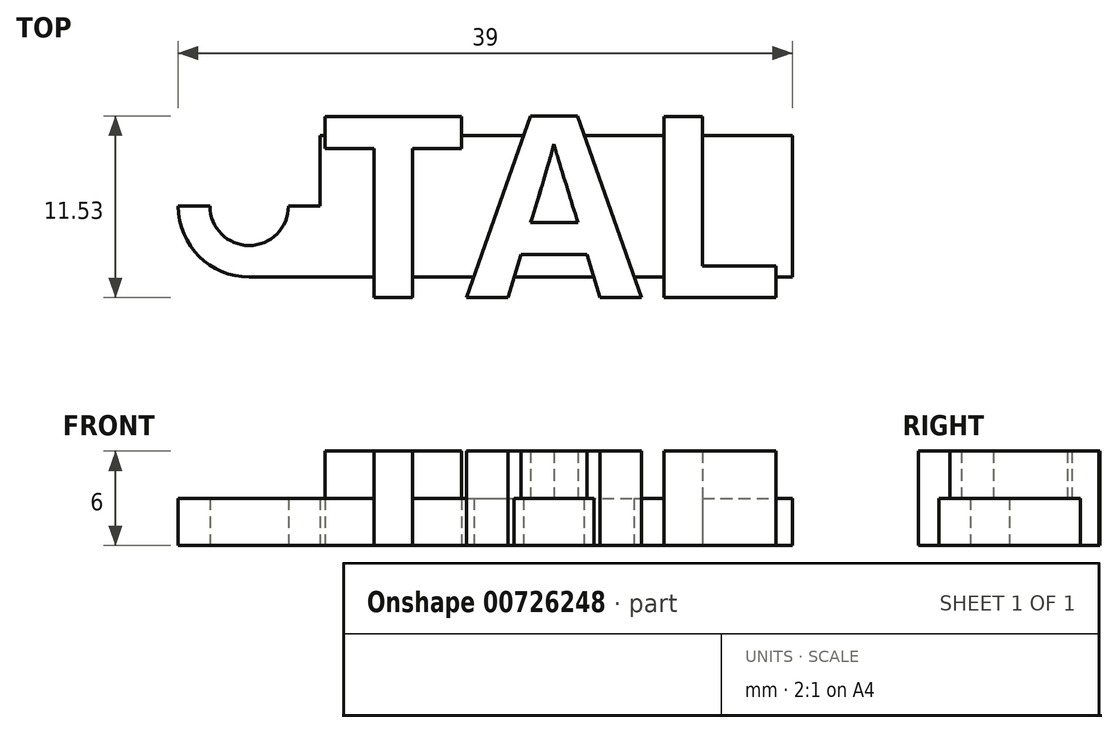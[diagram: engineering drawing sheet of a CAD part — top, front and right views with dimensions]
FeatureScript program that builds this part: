
annotation { "Feature Type Name" : "Feature", "Feature Type Description" : "" }
export const myFeature = defineFeature(function(context is Context, id is Id, definition is map)
    precondition{}
    {
        {
            var Q0;
            Q0=qCreatedBy(makeId("Top.planeOp"),FACE);
            var sketch = newSketch(context, id + "F0", { "sketchPlane" : qUnion([Q0])});
            skLineSegment(sketch, "E0.bottom", {"start": v(-15, -4.5) * mm, "end": v(15, -4.5) * mm});
            skLineSegment(sketch, "E0.top", {"start": v(-15, 4.5) * mm, "end": v(15, 4.5) * mm});
            skLineSegment(sketch, "E0.left", {"start": v(-15, -4.5) * mm, "end": v(-15, 4.5) * mm});
            skLineSegment(sketch, "E0.right", {"start": v(15, -4.5) * mm, "end": v(15, 4.5) * mm});
            skPoint(sketch, "E0.middle", {"position": v(0, 0) * mm});
            skText(sketch, "E1", { "text": "TAL", "fontName": "OpenSans-Bold.ttf"});
            skLineSegment(sketch, "E2", {"start": v(-15, 4.5) * mm, "end": v(-19.5, 4.5) * mm});
            skLineSegment(sketch, "E3", {"start": v(-19.5, -4.5) * mm, "end": v(-15, -4.5) * mm});
            skLineSegment(sketch, "E4", {"start": v(-24, 0) * mm, "end": v(-15, 0) * mm});
            skArc(sketch, "E5", {"start": v(-24, 0) * mm, "mid": v(-22.68, -3.18) * mm, "end": v(-19.5, -4.5) * mm});
            skArc(sketch, "E6", {"start": v(-24, 0) * mm, "mid": v(-22.68, 3.18) * mm, "end": v(-19.5, 4.5) * mm});
            skCircle(sketch, "E7", {"center": v(-19.5, 0) * mm, "radius": 2.5 * mm});
            skPoint(sketch, "E8.orphan", {"position": v(-24, -4.5) * mm});
            skPoint(sketch, "E9.orphan", {"position": v(-24, 4.5) * mm});
            skLineSegment(sketch, "E10", {"start": v(-19.5, 4.5) * mm, "end": v(-15, 4.5) * mm});
            const initialGuessF0  = {"E1": [-0.015, -0.0058, 1, 0, 0.01158]};
            skSetInitialGuess(sketch, initialGuessF0);
            skSolve(sketch);
        }
        {
            var Q0;
            {var subQ5=sQuery(id+"F0.wireOp",EDGE,"E5");Q0=makeQuery(id+"F0.imprint","IMPRINT",FACE,{"disambiguationData":[TD([[makeQuery(id+"F0.imprint","IMPRINT",EDGE,{"derivedFrom":subQ5}),1.0]])]});}
            var Q1;
            {var subQ7=sQuery(id+"F0.wireOp",EDGE,"E6");Q1=makeQuery(id+"F0.imprint","IMPRINT",FACE,{"disambiguationData":[TD([[makeQuery(id+"F0.imprint","IMPRINT",EDGE,{"derivedFrom":subQ7}),-1.0]])]});}
            var Q2;
            {var subQ10=sQuery(id+"F0.wireOp",EDGE,"E1.sketch_text.stroke-2");Q2=makeQuery(id+"F0.imprint","IMPRINT",FACE,{"disambiguationData":[TD([[makeQuery(id+"F0.imprint","IMPRINT",EDGE,{"derivedFrom":subQ10}),1.0]])]});}
            var Q3;
            {var subQ0=sQuery(id+"F0.wireOp",EDGE,"E1.sketch_text.stroke-6");Q3=makeQuery(id+"F0.imprint","IMPRINT",FACE,{"disambiguationData":[TD([[makeQuery(id+"F0.imprint","IMPRINT",EDGE,{"derivedFrom":subQ0}),1.0]])]});}
            var Q4;
            {var subQ5=sQuery(id+"F0.wireOp",EDGE,"E1.sketch_text.stroke-9");Q4=makeQuery(id+"F0.imprint","IMPRINT",FACE,{"disambiguationData":[TD([[makeQuery(id+"F0.imprint","IMPRINT",EDGE,{"derivedFrom":subQ5}),1.0]])]});}
            var Q5;
            Q5=makeQuery(id+"F0.imprint","IMPRINT",FACE,{"disambiguationData":[TD([[makeQuery(id+"F0.imprint","IMPRINT",EDGE,{"derivedFrom":sQuery(id+"F0.wireOp",EDGE,"E1.sketch_text.stroke-16")}),1.0]])]});
            var Q6;
            {var subQ0=sQuery(id+"F0.wireOp",EDGE,"E1.sketch_text.stroke-14");var subQ1=sQuery(id+"F0.wireOp",EDGE,"E0.bottom");var subQ2=makeQuery(id+"F0.imprint","INTERSECT",VERTEX,{"derivedFrom":[subQ1,subQ0]});Q6=makeQuery(id+"F0.imprint","IMPRINT",FACE,{"disambiguationData":[TD([[makeQuery(id+"F0.imprint","IMPRINT",EDGE,{"disambiguationData":[TD([[subQ2,-1.0]])],"derivedFrom":subQ1}),1.0]])]});}
            var Q7;
            {var subQ4=sQuery(id+"F0.wireOp",EDGE,"E0.right");Q7=makeQuery(id+"F0.imprint","IMPRINT",FACE,{"disambiguationData":[TD([[makeQuery(id+"F0.imprint","IMPRINT",EDGE,{"derivedFrom":subQ4}),1.0]])]});}
            extrude(context, id + "F1", {"entities" : qUnion([Q0, Q1, Q2, Q3, Q4, Q5, Q6, Q7]), "depth" : 3 * mm, "offsetDistance" : 25 * mm});
        }
        {
            var Q0;
            {var subQ0=sQuery(id+"F0.wireOp",EDGE,"E1.sketch_text.stroke-2");Q0=makeQuery(id+"F0.imprint","IMPRINT",FACE,{"disambiguationData":[TD([[makeQuery(id+"F0.imprint","IMPRINT",EDGE,{"derivedFrom":subQ0}),-1.0]])]});}
            var Q1;
            {var subQ5=sQuery(id+"F0.wireOp",EDGE,"E1.sketch_text.stroke-0");Q1=makeQuery(id+"F0.imprint","IMPRINT",FACE,{"disambiguationData":[TD([[makeQuery(id+"F0.imprint","IMPRINT",EDGE,{"derivedFrom":subQ5}),-1.0]])]});}
            var Q2;
            {var subQ5=sQuery(id+"F0.wireOp",EDGE,"E1.sketch_text.stroke-4");Q2=makeQuery(id+"F0.imprint","IMPRINT",FACE,{"disambiguationData":[TD([[makeQuery(id+"F0.imprint","IMPRINT",EDGE,{"derivedFrom":subQ5}),-1.0]])]});}
            var Q3;
            {var subQ5=sQuery(id+"F0.wireOp",EDGE,"E1.sketch_text.stroke-9");Q3=makeQuery(id+"F0.imprint","IMPRINT",FACE,{"disambiguationData":[TD([[makeQuery(id+"F0.imprint","IMPRINT",EDGE,{"derivedFrom":subQ5}),-1.0]])]});}
            var Q4;
            {var subQ5=sQuery(id+"F0.wireOp",EDGE,"E1.sketch_text.stroke-15");Q4=makeQuery(id+"F0.imprint","IMPRINT",FACE,{"disambiguationData":[TD([[makeQuery(id+"F0.imprint","IMPRINT",EDGE,{"derivedFrom":subQ5}),-1.0]])]});}
            var Q5;
            {var subQ5=sQuery(id+"F0.wireOp",EDGE,"E1.sketch_text.stroke-11");Q5=makeQuery(id+"F0.imprint","IMPRINT",FACE,{"disambiguationData":[TD([[makeQuery(id+"F0.imprint","IMPRINT",EDGE,{"derivedFrom":subQ5}),-1.0]])]});}
            var Q6;
            {var subQ5=sQuery(id+"F0.wireOp",EDGE,"E1.sketch_text.stroke-13");Q6=makeQuery(id+"F0.imprint","IMPRINT",FACE,{"disambiguationData":[TD([[makeQuery(id+"F0.imprint","IMPRINT",EDGE,{"derivedFrom":subQ5}),-1.0]])]});}
            var Q7;
            {var subQ5=sQuery(id+"F0.wireOp",EDGE,"E1.sketch_text.stroke-25");Q7=makeQuery(id+"F0.imprint","IMPRINT",FACE,{"disambiguationData":[TD([[makeQuery(id+"F0.imprint","IMPRINT",EDGE,{"derivedFrom":subQ5}),-1.0]])]});}
            var Q8;
            {var subQ5=sQuery(id+"F0.wireOp",EDGE,"E1.sketch_text.stroke-23");Q8=makeQuery(id+"F0.imprint","IMPRINT",FACE,{"disambiguationData":[TD([[makeQuery(id+"F0.imprint","IMPRINT",EDGE,{"derivedFrom":subQ5}),-1.0]])]});}
            var Q9;
            {var subQ5=sQuery(id+"F0.wireOp",EDGE,"E1.sketch_text.stroke-21");Q9=makeQuery(id+"F0.imprint","IMPRINT",FACE,{"disambiguationData":[TD([[makeQuery(id+"F0.imprint","IMPRINT",EDGE,{"derivedFrom":subQ5}),-1.0]])]});}
            extrude(context, id + "F2", {"entities" : qUnion([Q0, Q1, Q2, Q3, Q4, Q5, Q6, Q7, Q8, Q9]), "operationType" : NewBodyOperationType.ADD, "depth" : 6 * mm, "offsetDistance" : 25 * mm});
        }
    });
